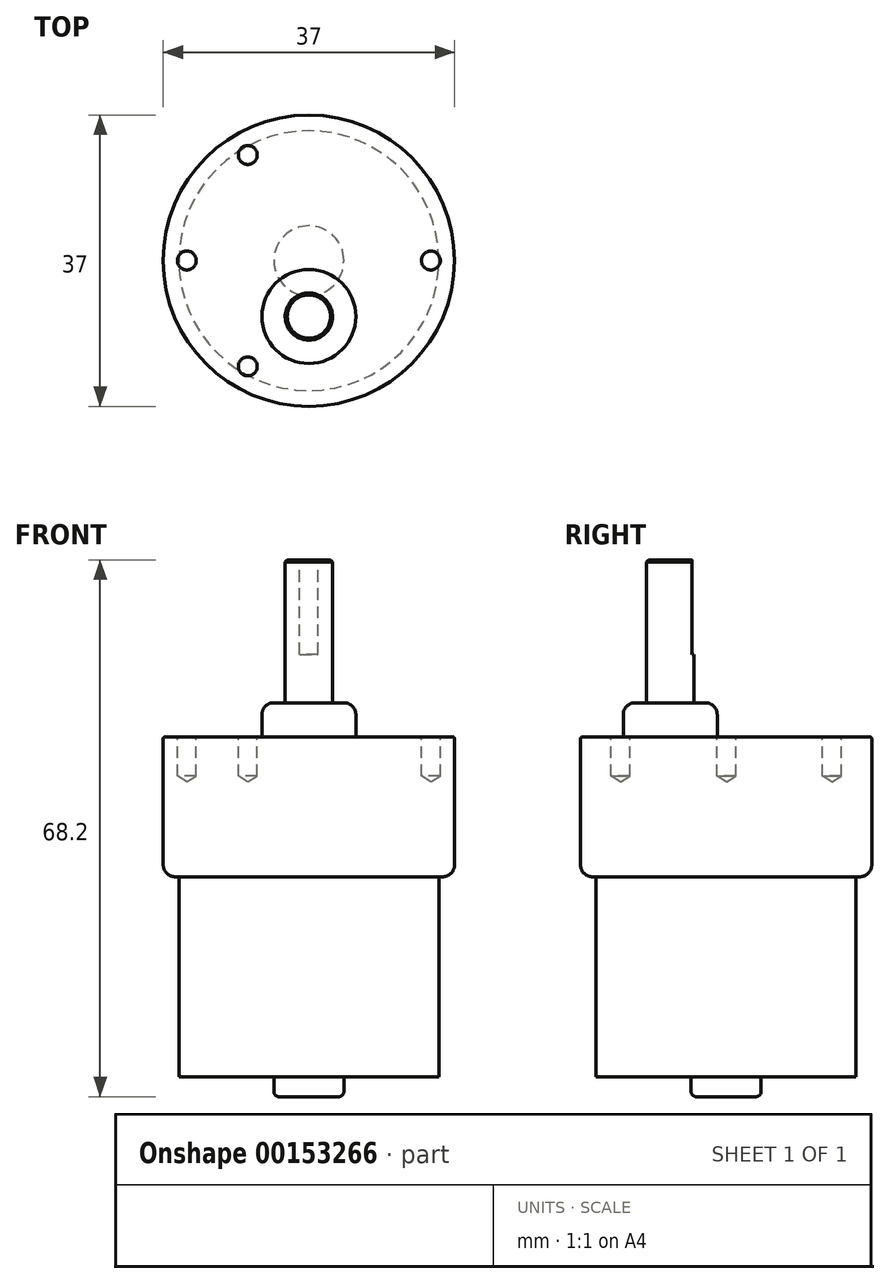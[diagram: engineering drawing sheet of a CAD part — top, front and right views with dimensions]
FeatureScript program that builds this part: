
annotation { "Feature Type Name" : "Feature", "Feature Type Description" : "" }
export const myFeature = defineFeature(function(context is Context, id is Id, definition is map)
    precondition{}
    {
        {
            var Q0;
            Q0=qCreatedBy(makeId("Top.planeOp"),FACE);
            var sketch = newSketch(context, id + "F0", { "sketchPlane" : qUnion([Q0])});
            skCircle(sketch, "E0", {"center": v(0, 0) * mm, "radius": 18.5 * mm});
            skCircle(sketch, "E1", {"center": v(0, 0) * mm, "radius": 16.51 * mm});
            skSolve(sketch);
        }
        {
            var Q0;
            Q0=makeQuery(id+"F0.imprint","IMPRINT",FACE,{"disambiguationData":[TD([[makeQuery(id+"F0.imprint","IMPRINT",EDGE,{"derivedFrom":sQuery(id+"F0.wireOp",EDGE,"E0")}),1.0]])]});
            var Q1;
            Q1=makeQuery(id+"F0.imprint","IMPRINT",FACE,{"disambiguationData":[TD([[makeQuery(id+"F0.imprint","IMPRINT",EDGE,{"derivedFrom":sQuery(id+"F0.wireOp",EDGE,"E1")}),1.0]])]});
            extrude(context, id + "F1", {"entities" : qUnion([Q0, Q1]), "depth" : 17.78 * mm});
        }
        {
            var Q0;
            Q0=makeQuery(id+"F1.opExtrude","CAP_FACE",FACE,{"disambiguationData":[OSD([sQuery(id+"F0.wireOp",EDGE,"E0")])],"isStart":false});
            var sketch = newSketch(context, id + "F2", { "sketchPlane" : qUnion([Q0])});
            skLineSegment(sketch, "E2", {"start": v(0, -18.5) * mm, "end": v(0, 18.5) * mm, "construction": true});
            skCircle(sketch, "E3", {"center": v(0, -7.1) * mm, "radius": 5.97 * mm});
            skCircle(sketch, "E4", {"center": v(0, 0) * mm, "radius": 15.5 * mm, "construction": true});
            skCircle(sketch, "E5", {"center": v(-7.76, 13.42) * mm, "radius": 1.5 * mm});
            skCircle(sketch, "E6", {"center": v(-7.76, -13.42) * mm, "radius": 1.5 * mm});
            skLineSegment(sketch, "E7", {"start": v(-7.76, 13.42) * mm, "end": v(-7.76, -13.42) * mm, "construction": true});
            skCircle(sketch, "E8", {"center": v(15.5, 0.02) * mm, "radius": 1.5 * mm});
            skLineSegment(sketch, "E9", {"start": v(-7.76, 13.42) * mm, "end": v(15.5, 0.02) * mm, "construction": true});
            skLineSegment(sketch, "E10", {"start": v(15.5, 0.02) * mm, "end": v(-15.5, 0.02) * mm, "construction": true});
            skCircle(sketch, "E11", {"center": v(-15.5, 0.02) * mm, "radius": 1.5 * mm});
            skSolve(sketch);
        }
        {
            var Q0;
            Q0=makeQuery(id+"F2.imprint","IMPRINT",FACE,{"disambiguationData":[TD([[makeQuery(id+"F2.imprint","IMPRINT",EDGE,{"derivedFrom":sQuery(id+"F2.wireOp",EDGE,"E3")}),1.0]])]});
            extrude(context, id + "F3", {"entities" : qUnion([Q0]), "operationType" : NewBodyOperationType.ADD, "depth" : 4.32 * mm});
        }
        {
            var Q0;
            Q0=makeQuery(id+"F3.opExtrude","CAP_FACE",FACE,{"disambiguationData":[OSD([sQuery(id+"F2.wireOp",EDGE,"E3")])],"isStart":false});
            var sketch = newSketch(context, id + "F4", { "sketchPlane" : qUnion([Q0])});
            skCircle(sketch, "E12", {"center": v(0, -7.1) * mm, "radius": 3 * mm});
            skSolve(sketch);
        }
        {
            var Q0;
            Q0=makeQuery(id+"F4.imprint","IMPRINT",FACE,{"disambiguationData":[TD([[makeQuery(id+"F4.imprint","IMPRINT",EDGE,{"derivedFrom":sQuery(id+"F4.wireOp",EDGE,"E12")}),1.0]])]});
            extrude(context, id + "F5", {"entities" : qUnion([Q0]), "depth" : 18.16 * mm});
        }
        {
            var Q0;
            Q0=makeQuery(id+"F5.opExtrude","CAP_FACE",FACE,{"disambiguationData":[OSD([sQuery(id+"F4.wireOp",EDGE,"E12")])],"isStart":false});
            var sketch = newSketch(context, id + "F6", { "sketchPlane" : qUnion([Q0])});
            skLineSegment(sketch, "E13", {"start": v(-1.2, -4.34) * mm, "end": v(1.2, -4.34) * mm});
            skPoint(sketch, "E14", {"position": v(0, -4.34) * mm});
            skLineSegment(sketch, "E15", {"start": v(0, -7.1) * mm, "end": v(0, -4.34) * mm, "construction": true});
            skSolve(sketch);
        }
        {
            var Q0;
            {var subQ0=sQuery(id+"F6.wireOp",EDGE,"E13");Q0=makeQuery(id+"F6.imprint","IMPRINT",FACE,{"disambiguationData":[TD([[makeQuery(id+"F6.imprint","IMPRINT",EDGE,{"derivedFrom":subQ0}),1.0]])]});}
            extrude(context, id + "F7", {"entities" : qUnion([Q0]), "operationType" : NewBodyOperationType.REMOVE, "oppositeDirection" : true, "depth" : 12 * mm});
        }
        {
            var Q0;
            Q0=makeQuery(id+"F0.imprint","IMPRINT",FACE,{"disambiguationData":[TD([[makeQuery(id+"F0.imprint","IMPRINT",EDGE,{"derivedFrom":sQuery(id+"F0.wireOp",EDGE,"E1")}),1.0]])]});
            extrude(context, id + "F8", {"entities" : qUnion([Q0]), "operationType" : NewBodyOperationType.ADD, "oppositeDirection" : true, "depth" : 25.4 * mm});
        }
        {
            var Q0;
            Q0=makeQuery(id+"F8.opExtrude","CAP_FACE",FACE,{"disambiguationData":[OSD([sQuery(id+"F0.wireOp",EDGE,"E1")])],"isStart":false});
            var sketch = newSketch(context, id + "F9", { "sketchPlane" : qUnion([Q0])});
            skCircle(sketch, "E16", {"center": v(0, 0) * mm, "radius": 4.45 * mm});
            skSolve(sketch);
        }
        {
            var Q0;
            Q0=makeQuery(id+"F9.imprint","IMPRINT",FACE,{"disambiguationData":[TD([[makeQuery(id+"F9.imprint","IMPRINT",EDGE,{"derivedFrom":sQuery(id+"F9.wireOp",EDGE,"E16")}),1.0]])]});
            extrude(context, id + "F10", {"entities" : qUnion([Q0]), "operationType" : NewBodyOperationType.ADD, "depth" : 2.54 * mm});
        }
        {
            var Q0;
            Q0=makeQuery(id+"F10.opExtrude","CAP_EDGE",EDGE,{"disambiguationData":[OSD([sQuery(id+"F9.wireOp",EDGE,"E16")])],"isStart":false});
            fillet(context, id + "F11", {"entities" : qUnion([Q0]), "radius" : 0.64 * mm, "tangentPropagation" : true, "allowEdgeOverflow" : false});
        }
        {
            var Q0;
            Q0=makeQuery(id+"F1.opExtrude","CAP_EDGE",EDGE,{"disambiguationData":[OSD([sQuery(id+"F0.wireOp",EDGE,"E0")])],"isStart":true});
            fillet(context, id + "F12", {"entities" : qUnion([Q0]), "radius" : 1.5 * mm, "tangentPropagation" : true, "allowEdgeOverflow" : false});
        }
        {
            var Q0;
            Q0=makeQuery(id+"F3.opExtrude","CAP_EDGE",EDGE,{"disambiguationData":[OSD([sQuery(id+"F2.wireOp",EDGE,"E3")])],"isStart":false});
            fillet(context, id + "F13", {"entities" : qUnion([Q0]), "radius" : 1.5 * mm, "tangentPropagation" : true, "allowEdgeOverflow" : false});
        }
        {
            var Q0;
            Q0=makeQuery(id+"F1.opExtrude","CAP_EDGE",EDGE,{"disambiguationData":[OSD([sQuery(id+"F0.wireOp",EDGE,"E0")])],"isStart":false});
            fillet(context, id + "F14", {"entities" : qUnion([Q0]), "radius" : 0.25 * mm, "tangentPropagation" : true, "allowEdgeOverflow" : false});
        }
        {
            var Q0;
            Q0=makeQuery(id+"F5.opExtrude","CAP_EDGE",EDGE,{"disambiguationData":[OSD([sQuery(id+"F4.wireOp",EDGE,"E12")])],"isStart":false});
            chamfer(context, id + "F15", {"entities" : qUnion([Q0]), "width" : 0.25 * mm, "tangentPropagation" : true});
        }
        {
            var Q0;
            Q0=sQuery(id+"F2.wireOp",VERTEX,"E9.start");
            var Q1;
            Q1=sQuery(id+"F2.wireOp",VERTEX,"E7.end");
            var Q2;
            Q2=sQuery(id+"F2.wireOp",VERTEX,"E9.end");
            var Q3;
            Q3=sQuery(id+"F2.wireOp",VERTEX,"E11.center");
            var Q4;
            Q4=makeQuery(id+"F1.opExtrude","SWEPT_BODY",BODY,{"disambiguationData":[OSD([sQuery(id+"F0.wireOp",EDGE,"E0")])]});
            hole(context, id + "F16", {"style" : HoleStyle.SIMPLE, "endStyle" : HoleEndStyle.BLIND, "standardTappedOrClearance" : lookupTablePath({ "standard" : "ISO", "engagement" : "75%", "pitch" : "0.6 mm", "size" : "M3", "type" : "Tapped" }), "standardBlindInLast" : lookupTablePath({ "standard" : "ISO", "engagement" : "75%", "pitch" : "0.6 mm", "size" : "M3", "type" : "Tapped" }), "holeDiameter" : 2.4 * mm, "holeDepth" : 5 * mm, "startFromSketch" : true, "locations" : qUnion([Q0, Q1, Q2, Q3]), "scope" : qUnion([Q4])});
        }
    });
